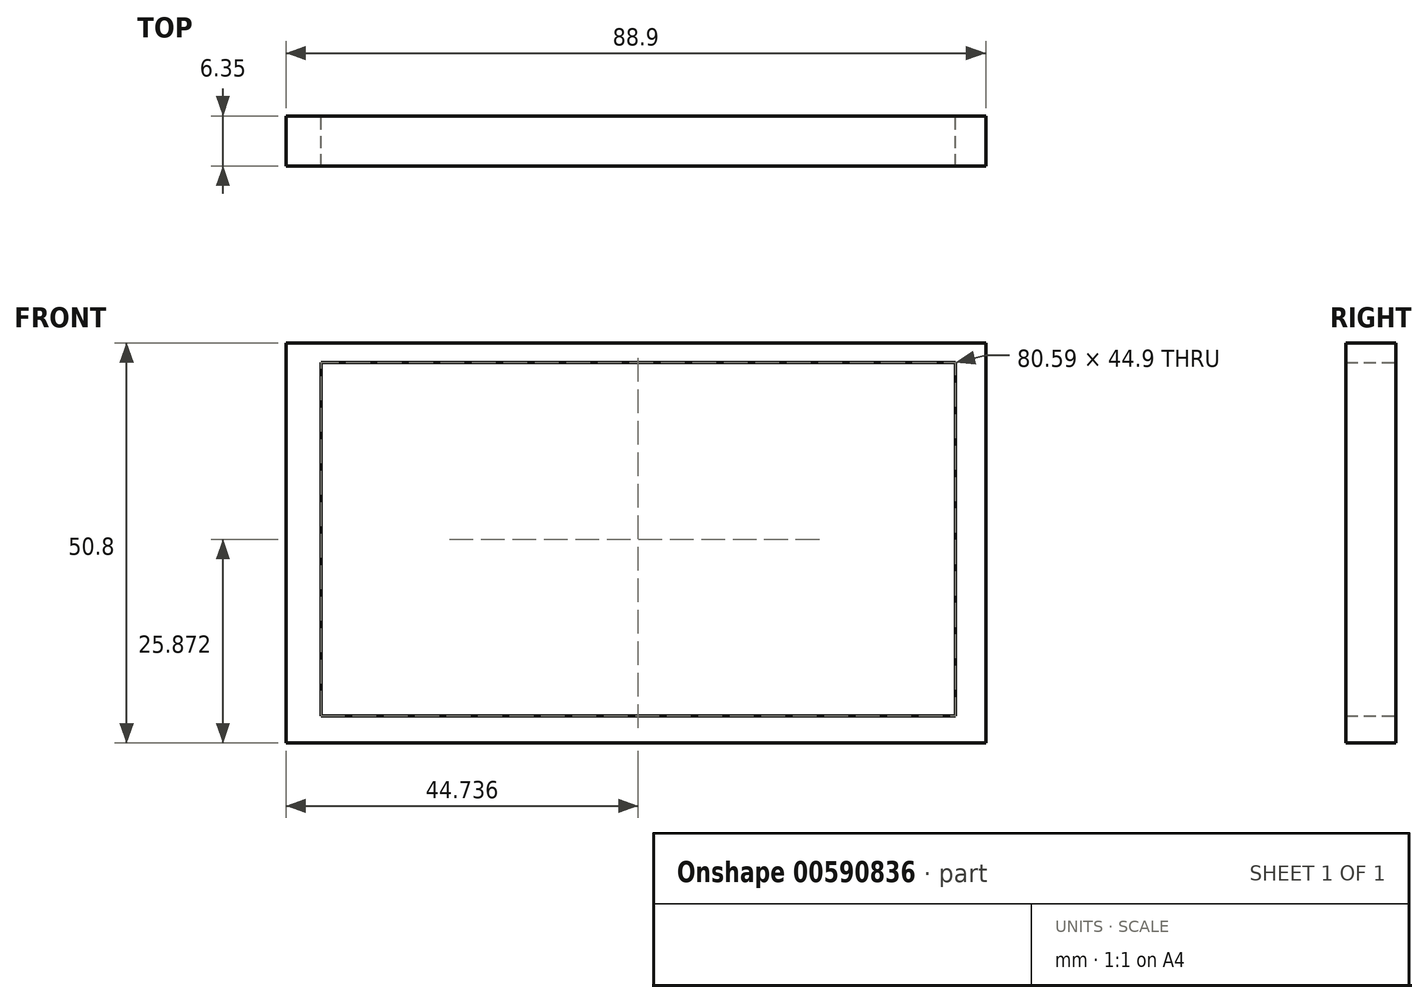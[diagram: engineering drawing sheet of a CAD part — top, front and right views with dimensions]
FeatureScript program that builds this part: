
annotation { "Feature Type Name" : "Feature", "Feature Type Description" : "" }
export const myFeature = defineFeature(function(context is Context, id is Id, definition is map)
    precondition{}
    {
        {
            var Q0;
            Q0=qCreatedBy(makeId("Front.planeOp"),FACE);
            var sketch = newSketch(context, id + "F0", { "sketchPlane" : qUnion([Q0])});
            skLineSegment(sketch, "E0.bottom", {"start": v(-35.67, 33.13) * mm, "end": v(53.23, 33.13) * mm});
            skLineSegment(sketch, "E0.top", {"start": v(-35.67, -17.67) * mm, "end": v(53.23, -17.67) * mm});
            skLineSegment(sketch, "E0.left", {"start": v(-35.67, 33.13) * mm, "end": v(-35.67, -17.67) * mm});
            skLineSegment(sketch, "E0.right", {"start": v(53.23, 33.13) * mm, "end": v(53.23, -17.67) * mm});
            skLineSegment(sketch, "E1.bottom", {"start": v(-31.23, 30.65) * mm, "end": v(49.36, 30.65) * mm});
            skLineSegment(sketch, "E1.top", {"start": v(-31.23, -14.25) * mm, "end": v(49.36, -14.25) * mm});
            skLineSegment(sketch, "E1.left", {"start": v(-31.23, 30.65) * mm, "end": v(-31.23, -14.25) * mm});
            skLineSegment(sketch, "E1.right", {"start": v(49.36, 30.65) * mm, "end": v(49.36, -14.25) * mm});
            skSolve(sketch);
        }
        {
            var Q0;
            Q0=makeQuery(id+"F0.imprint","IMPRINT",FACE,{"disambiguationData":[TD([[makeQuery(id+"F0.imprint","IMPRINT",EDGE,{"derivedFrom":sQuery(id+"F0.wireOp",EDGE,"E0.bottom")}),-1.0]])]});
            extrude(context, id + "F1", {"entities" : qUnion([Q0]), "depth" : 6.35 * mm, "offsetDistance" : 25.4 * mm});
        }
        {
            var Q0;
            Q0=sQuery(id+"F0.wireOp",EDGE,"E1.left");
            var Q1;
            Q1=sQuery(id+"F0.wireOp",EDGE,"E1.top");
            var Q2;
            Q2=sQuery(id+"F0.wireOp",EDGE,"E1.right");
            var Q3;
            Q3=sQuery(id+"F0.wireOp",EDGE,"E1.bottom");
            extrude(context, id + "F2", {"bodyType" : ToolBodyType.SURFACE, "surfaceEntities" : qUnion([Q0, Q1, Q2, Q3]), "depth" : 5.08 * mm, "offsetDistance" : 25.4 * mm});
        }
    });
